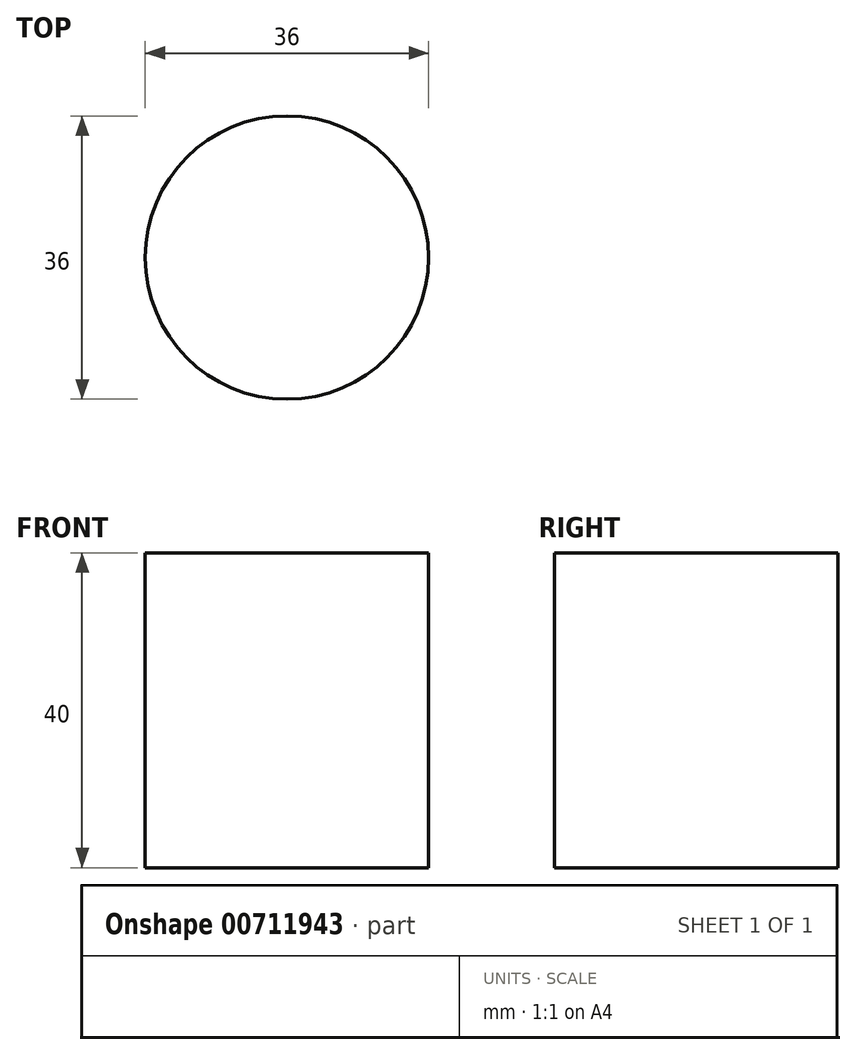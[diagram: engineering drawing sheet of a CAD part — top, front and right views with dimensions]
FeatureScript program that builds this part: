
annotation { "Feature Type Name" : "Feature", "Feature Type Description" : "" }
export const myFeature = defineFeature(function(context is Context, id is Id, definition is map)
    precondition{}
    {
        {
            var Q0;
            Q0=qCreatedBy(makeId("Top.planeOp"),FACE);
            var sketch = newSketch(context, id + "F0", { "sketchPlane" : qUnion([Q0])});
            skCircle(sketch, "E0", {"center": v(0, 0) * mm, "radius": 18 * mm});
            skSolve(sketch);
        }
        {
            var Q0;
            Q0=qSketchRegion(id+"F0",true);
            extrude(context, id + "F1", {"entities" : qUnion([Q0]), "depth" : 40 * mm, "offsetDistance" : 25 * mm});
        }
    });
